FCSTD DOCUMENT  (FreeCAD 1.1R20251031 (Git shallow))
Label: generated_example_K93-10436_all7_withDockLinkFrame
License: All rights reserved
LicenseURL: https://en.wikipedia.org/wiki/All_rights_reserved
objects: App::FeaturePython×18, App::Link×15, App::Point×2, Assembly::AssemblyLink×1, Assembly::JointGroup×1, Assembly::AssemblyObject×1
EXTERNAL_REF file=K93-10436-H7-L120.FCStd obj=K93_120
EXTERNAL_REF file=Reference_all7.FCStd obj=Reference_all7_1
EXTERNAL_REF file=K93-10436-H7-L120_frontpanel_generated_example.FCStd obj=Body
EXTERNAL_REF file=K93-10436-H7-L120_Tarantinorino_right_withFeet.FCStd obj=Assembly
EXTERNAL_REF file=K93-10436-H7-L120_DockLink_Frame_example_mirrored.FCStd obj=Part__Mirroring
EXTERNAL_REF file=K93-10436-H7-L120_Bumperino.FCStd obj=Body
EXTERNAL_REF file=K93-10436-H7-L120_DockLink_Frame_example.FCStd obj=Body
EXTERNAL_REF file=3M_SJ5382.FCStd obj=Body

FEATURE [App::Link] K93_120  label="K93-120"
  LinkPlacement = pos=(0,126.938,111.562) rot=(1,0,0;1.5708rad)
  LinkedObject = -> <external K93-10436-H7-L120.FCStd>#K93_120
  Placement = pos=(0,126.938,111.562) rot=(1,0,0;1.5708rad)
FEATURE [App::FeaturePython] GroundedJoint  # Assembly grounded joint (typed FeaturePython)
  ObjectToGround = -> K93_120
  Placement = pos=(0,126.938,111.562) rot=(1,0,0;1.5708rad)
FEATURE [App::Link] Reference_all7_1  label="Reference_all7 1"
  LinkPlacement = pos=(2.87919,6.93809,110.59) rot=(0.99808,0,0;0rad)
  LinkedObject = -> <external Reference_all7.FCStd>#Reference_all7_1
  Placement = pos=(2.87919,6.93809,110.59) rot=(0.99808,0,0;0rad)
FEATURE [App::FeaturePython] Joint  label="Distance"  # Assembly joint (typed FeaturePython)
  Angle = 0
  AngleMax = 0
  AngleMin = 0
  Detach1 = false
  Detach2 = false
  Distance = -0.2
  Distance2 = 0
  EnableAngleMax = false
  EnableAngleMin = false
  EnableLengthMax = false
  EnableLengthMin = false
  JointType = 5 (Distance)
  LengthMax = 0
  LengthMin = 0
  Offset1 = pos=(0,0,0) rot=(0,0,1;3.14159rad)
  Placement1 = pos=(-50,10.1,0) rot=(-0.707107,0,0.707107;3.14159rad)
  Placement2 = pos=(-49.8,1.8e-15,0.755) rot=(-0.57735,-0.57735,0.57735;2.0944rad)
  Reference1 = -> Assembly [K93_120.Part__Feature.Face87,K93_120.Part__Feature.Vertex159]
  Reference2 = -> Assembly [Reference_all7_1.Part__Feature426.Face3,Reference_all7_1.Part__Feature426.Vertex3]
  Suppressed = false
FEATURE [App::FeaturePython] Joint001  label="Distance001"  # Assembly joint (typed FeaturePython)
  Angle = 0
  AngleMax = 0
  AngleMin = 0
  Detach1 = false
  Detach2 = false
  Distance = 0.2
  Distance2 = 0
  EnableAngleMax = false
  EnableAngleMin = false
  EnableLengthMax = false
  EnableLengthMin = false
  JointType = 5 (Distance)
  LengthMax = 0
  LengthMin = 0
  Placement1 = pos=(4e-16,-59.8,0.755) rot=(0,-0.707107,0.707107;3.14159rad)
  Placement2 = pos=(1.58751,4.42551,60) rot=(0,0,1;0rad)
  Reference1 = -> Assembly [Reference_all7_1.Part__Feature426.Face1,Reference_all7_1.Part__Feature426.Vertex4]
  Reference2 = -> Assembly [K93_120.Part__Feature.Face58,K93_120.Part__Feature.Vertex116]
  Suppressed = false
FEATURE [App::FeaturePython] Joint002  label="Distance002"  # Assembly joint (typed FeaturePython)
  Angle = 0
  AngleMax = 0
  AngleMin = 0
  Detach1 = false
  Detach2 = false
  Distance = 0.25
  Distance2 = 0
  EnableAngleMax = false
  EnableAngleMin = false
  EnableLengthMax = false
  EnableLengthMin = false
  JointType = 5 (Distance)
  LengthMax = 0
  LengthMin = 0
  Placement1 = pos=(-48.85,11.1,0) rot=(-0.57735,-0.57735,0.57735;4.18879rad)
  Placement2 = pos=(0.0111337,0.109635,1.51) rot=(0,0,1;0rad)
  Reference1 = -> Assembly [K93_120.Part__Feature.Face78,K93_120.Part__Feature.Vertex160]
  Reference2 = -> Assembly [Reference_all7_1.Part__Feature426.Face5,Reference_all7_1.Part__Feature426.Vertex3]
  Suppressed = false
FEATURE [App::Link] Body
  LinkPlacement = pos=(2.87919,-53.8119,119.256) rot=(1,0,0;1.5708rad)
  LinkedObject = -> <external K93-10436-H7-L120_frontpanel_generated_example.FCStd>#Body
  Placement = pos=(2.87919,-53.8119,119.256) rot=(1,0,0;1.5708rad)
FEATURE [App::FeaturePython] Joint003  label="Fixed"  # Assembly joint (typed FeaturePython)
  Angle = 0
  AngleMax = 0
  AngleMin = 0
  Detach1 = false
  Detach2 = false
  Distance = 0
  Distance2 = 0
  EnableAngleMax = false
  EnableAngleMin = false
  EnableLengthMax = false
  EnableLengthMin = false
  JointType = 0 (Fixed)
  LengthMax = 0
  LengthMin = 0
  Offset2 = pos=(0,0,0) rot=(0,0,1;3.14159rad)
  Placement1 = pos=(9.8e-15,0,60) rot=(0.707107,0,0.707107;3.14159rad)
  Placement2 = pos=(1.5046e-12,17.9943,-0.75) rot=(0,1,0;4.71239rad)
  Reference1 = -> Assembly [K93_120.Part__Feature001.Edge190,K93_120.Part__Feature001.Edge190]
  Reference2 = -> Assembly [Body.Edge39,Body.Edge39]
  Suppressed = false
FEATURE [App::Point] Origin001  label="Origin"
  Role = Origin
FEATURE [Assembly::AssemblyLink] Assembly004  label="Assembly"
  LinkedObject = -> <external K93-10436-H7-L120_Tarantinorino_right_withFeet.FCStd>#Assembly
  Origin = -> Origin008
  Placement = pos=(2.83915,-40.6619,129.251) rot=(0,0,1;0rad)
  Rigid = true
FEATURE [App::Point] Origin009  label="Origin011"
  Role = Origin
FEATURE [App::FeaturePython] Joint008  label="Fixed005"  # Assembly joint (typed FeaturePython)
  Angle = 0
  AngleMax = 0
  AngleMin = 0
  Detach1 = false
  Detach2 = false
  Distance = 0
  Distance2 = 0
  EnableAngleMax = false
  EnableAngleMin = false
  EnableLengthMax = false
  EnableLengthMin = false
  JointType = 0 (Fixed)
  LengthMax = 0
  LengthMin = 0
  Offset2 = pos=(0,0,0) rot=(0,0,1;3.14159rad)
  Placement2 = pos=(-47.3,-11.9443,0.75) rot=(0,1,0;3.14159rad)
  Reference1 = -> Assembly [Assembly004.Body__Mirror__1_001.Edge31,Assembly004.Body__Mirror__1_001.Edge31]
  Reference2 = -> Assembly [Body.Edge23,Body.Edge23]
  Suppressed = false
FEATURE [App::Link] Body__Mirror__1_  label="Body (Mirror #1)"
  LinkPlacement = pos=(2.85919,57.5381,130.16) rot=(0.998926,0,0;0rad)
  LinkedObject = -> <external K93-10436-H7-L120_DockLink_Frame_example_mirrored.FCStd>#Part__Mirroring
  Placement = pos=(2.85919,57.5381,130.16) rot=(0.998926,0,0;0rad)
FEATURE [App::FeaturePython] Joint009  label="Fixed010"  # Assembly joint (typed FeaturePython)
  Angle = 0
  AngleMax = 0
  AngleMin = 0
  Detach1 = false
  Detach2 = false
  Distance = 0
  Distance2 = 0
  EnableAngleMax = false
  EnableAngleMin = false
  EnableLengthMax = false
  EnableLengthMin = false
  JointType = 0 (Fixed)
  LengthMax = 0
  LengthMin = 0
  Offset2 = pos=(0,0,0) rot=(0,0,1;3.14159rad)
  Placement1 = pos=(-47.3,11.9443,0.75) rot=(-1,0,0;3.14159rad)
  Placement2 = pos=(47.32,10.9,1.04) rot=(0,-0.706347,0.706347;3.14159rad)
  Reference1 = -> Assembly [K93_120.Part__Feature003.Edge2,K93_120.Part__Feature003.Edge2]
  Reference2 = -> Assembly [Body__Mirror__1_.?Edge40,Body__Mirror__1_.?Edge40]
  Suppressed = false
FEATURE [App::Link] Body001
  LinkPlacement = pos=(2.87919,-56.1619,119.256) rot=(1,0,0;1.5708rad)
  LinkedObject = -> <external K93-10436-H7-L120_Bumperino.FCStd>#Body
  Placement = pos=(2.87919,-56.1619,119.256) rot=(1,0,0;1.5708rad)
FEATURE [App::Link] Body002
  LinkPlacement = pos=(2.87919,70.0381,119.256) rot=(0,0.707107,0.707107;3.14159rad)
  LinkedObject = -> <external K93-10436-H7-L120_Bumperino.FCStd>#Body
  Placement = pos=(2.87919,70.0381,119.256) rot=(0,0.707107,0.707107;3.14159rad)
FEATURE [App::Link] Body003
  LinkPlacement = pos=(2.83919,70.0381,119.256) rot=(-1,0,0;1.5708rad)
  LinkedObject = -> <external K93-10436-H7-L120_Bumperino.FCStd>#Body
  Placement = pos=(2.83919,70.0381,119.256) rot=(-1,0,0;1.5708rad)
FEATURE [App::Link] Body004
  LinkPlacement = pos=(2.91919,-56.1619,119.256) rot=(0,0.707107,-0.707107;3.14159rad)
  LinkedObject = -> <external K93-10436-H7-L120_Bumperino.FCStd>#Body
  Placement = pos=(2.91919,-56.1619,119.256) rot=(0,0.707107,-0.707107;3.14159rad)
FEATURE [App::FeaturePython] Joint012  label="Fixed013"  # Assembly joint (typed FeaturePython)
  Angle = 0
  AngleMax = 0
  AngleMin = 0
  Detach1 = false
  Detach2 = false
  Distance = 0
  Distance2 = 0
  EnableAngleMax = false
  EnableAngleMin = false
  EnableLengthMax = false
  EnableLengthMin = false
  JointType = 0 (Fixed)
  LengthMax = 0
  LengthMin = 0
  Placement1 = pos=(-47.32,12.5,1.04) rot=(0.998926,0,0;1.5708rad)
  Placement2 = pos=(-47.3,-11.9443,-1.42e-14) rot=(1,0,0;3.14159rad)
  Reference1 = -> Assembly [Body__Mirror__1_.?Edge65,Body__Mirror__1_.?Edge65]
  Reference2 = -> Assembly [Body003.Edge23,Body003.Edge23]
  Suppressed = false
FEATURE [App::FeaturePython] Joint013  label="Fixed014"  # Assembly joint (typed FeaturePython)
  Angle = 0
  AngleMax = 0
  AngleMin = 0
  Detach1 = false
  Detach2 = false
  Distance = 0
  Distance2 = 0
  EnableAngleMax = false
  EnableAngleMin = false
  EnableLengthMax = false
  EnableLengthMin = false
  JointType = 0 (Fixed)
  LengthMax = 0
  LengthMin = 0
  Offset2 = pos=(0,0,0) rot=(0,0,1;3.14159rad)
  Placement1 = pos=(47.32,12.5,1.04) rot=(0.998926,0,0;1.5708rad)
  Placement2 = pos=(-47.3,11.9443,-1.42e-14) rot=(0,0,1;3.14159rad)
  Reference1 = -> Assembly [Body__Mirror__1_.?Edge66,Body__Mirror__1_.?Edge66]
  Reference2 = -> Assembly [Body002.Edge22,Body002.Edge22]
  Suppressed = false
FEATURE [App::Link] Body005
  LinkPlacement = pos=(2.89919,-43.6619,130.16) rot=(0,0,1;0rad)
  LinkedObject = -> <external K93-10436-H7-L120_DockLink_Frame_example.FCStd>#Body
  Placement = pos=(2.89919,-43.6619,130.16) rot=(0,0,1;0rad)
FEATURE [App::FeaturePython] Joint014  label="Fixed016"  # Assembly joint (typed FeaturePython)
  Angle = 0
  AngleMax = 0
  AngleMin = 0
  Detach1 = false
  Detach2 = false
  Distance = 0
  Distance2 = 0
  EnableAngleMax = false
  EnableAngleMin = false
  EnableLengthMax = false
  EnableLengthMin = false
  JointType = 0 (Fixed)
  LengthMax = 0
  LengthMin = 0
  Placement1 = pos=(-47.3,11.9443,0.75) rot=(-1,0,0;3.14159rad)
  Placement2 = pos=(-47.32,-10.9,1.04) rot=(1,0,0;1.5708rad)
  Reference1 = -> Assembly [Body.Edge2,Body.Edge2]
  Reference2 = -> Assembly [Body005.?Edge39,Body005.?Edge39]
  Suppressed = false
FEATURE [App::FeaturePython] Joint015  label="Fixed017"  # Assembly joint (typed FeaturePython)
  Angle = 0
  AngleMax = 0
  AngleMin = 0
  Detach1 = false
  Detach2 = false
  Distance = 0
  Distance2 = 0
  EnableAngleMax = false
  EnableAngleMin = false
  EnableLengthMax = false
  EnableLengthMin = false
  JointType = 0 (Fixed)
  LengthMax = 0
  LengthMin = 0
  Placement1 = pos=(-47.32,-12.5,1.04) rot=(1,0,0;1.5708rad)
  Placement2 = pos=(-47.3,11.9443,7.1e-15) rot=(0,0,1;0rad)
  Reference1 = -> Assembly [Body005.?Edge65,Body005.?Edge65]
  Reference2 = -> Assembly [Body001.Edge22,Body001.Edge22]
  Suppressed = false
FEATURE [App::FeaturePython] Joint016  label="Fixed018"  # Assembly joint (typed FeaturePython)
  Angle = 0
  AngleMax = 0
  AngleMin = 0
  Detach1 = false
  Detach2 = false
  Distance = 0
  Distance2 = 0
  EnableAngleMax = false
  EnableAngleMin = false
  EnableLengthMax = false
  EnableLengthMin = false
  JointType = 0 (Fixed)
  LengthMax = 0
  LengthMin = 0
  Offset2 = pos=(0,0,0) rot=(0,0,1;3.14159rad)
  Placement1 = pos=(47.32,-12.5,1.04) rot=(1,0,0;1.5708rad)
  Placement2 = pos=(-47.3,-11.9443,0) rot=(0,1,0;3.14159rad)
  Reference1 = -> Assembly [Body005.?Edge66,Body005.?Edge66]
  Reference2 = -> Assembly [Body004.Face22,Body004.Edge1]
  Suppressed = false
FEATURE [App::Link] _3M_SJ5382  label="3M_SJ5382"
  LinkPlacement = pos=(37.4634,57.5381,91.16) rot=(1,0,0;3.14159rad)
  LinkedObject = -> <external 3M_SJ5382.FCStd>#Body
  Placement = pos=(37.4634,57.5381,91.16) rot=(1,0,0;3.14159rad)
FEATURE [App::Link] _3M_SJ5383  label="3M_SJ5383"
  LinkPlacement = pos=(-31.705,-43.6619,91.16) rot=(0,1,0;3.14159rad)
  LinkedObject = -> <external 3M_SJ5382.FCStd>#Body
  Placement = pos=(-31.705,-43.6619,91.16) rot=(0,1,0;3.14159rad)
FEATURE [App::Link] _3M_SJ5384  label="3M_SJ5384"
  LinkPlacement = pos=(-31.745,57.5381,91.16) rot=(1,0,0;3.14159rad)
  LinkedObject = -> <external 3M_SJ5382.FCStd>#Body
  Placement = pos=(-31.745,57.5381,91.16) rot=(1,0,0;3.14159rad)
FEATURE [App::Link] _3M_SJ5385  label="3M_SJ5385"
  LinkPlacement = pos=(37.5034,-43.6619,91.16) rot=(0,1,0;3.14159rad)
  LinkedObject = -> <external 3M_SJ5382.FCStd>#Body
  Placement = pos=(37.5034,-43.6619,91.16) rot=(0,1,0;3.14159rad)
FEATURE [App::Link] _3M_SJ5386  label="3M_SJ5386"
  LinkPlacement = pos=(-59.305,-43.6619,119.26) rot=(-0.707107,0,0.707107;3.14159rad)
  LinkedObject = -> <external 3M_SJ5382.FCStd>#Body
  Placement = pos=(-59.305,-43.6619,119.26) rot=(-0.707107,0,0.707107;3.14159rad)
FEATURE [App::Link] _3M_SJ5387  label="3M_SJ5387"
  LinkPlacement = pos=(-59.345,57.5381,119.26) rot=(-0.707107,0,0.707107;3.14159rad)
  LinkedObject = -> <external 3M_SJ5382.FCStd>#Body
  Placement = pos=(-59.345,57.5381,119.26) rot=(-0.707107,0,0.707107;3.14159rad)
FEATURE [App::FeaturePython] Joint017  label="Fixed019"  # Assembly joint (typed FeaturePython)
  Angle = 0
  AngleMax = 0
  AngleMin = 0
  Detach1 = false
  Detach2 = false
  Distance = 0
  Distance2 = 0
  EnableAngleMax = false
  EnableAngleMin = false
  EnableLengthMax = false
  EnableLengthMin = false
  JointType = 0 (Fixed)
  LengthMax = 0
  LengthMin = 0
  Placement1 = pos=(-34.6042,4.61512e-06,-39) rot=(0,1,0;3.14159rad)
  Placement2 = pos=(0,0,0) rot=(-1,0,0;3.14159rad)
  Reference1 = -> Assembly [Body005.?Face255,Body005.?Face255]
  Reference2 = -> Assembly [_3M_SJ5383.Edge4,_3M_SJ5383.Edge4]
  Suppressed = false
FEATURE [App::FeaturePython] Joint018  label="Fixed020"  # Assembly joint (typed FeaturePython)
  Angle = 0
  AngleMax = 0
  AngleMin = 0
  Detach1 = false
  Detach2 = false
  Distance = 0
  Distance2 = 0
  EnableAngleMax = false
  EnableAngleMin = false
  EnableLengthMax = false
  EnableLengthMin = false
  JointType = 0 (Fixed)
  LengthMax = 0
  LengthMin = 0
  Placement1 = pos=(34.6042,4.61512e-06,-39) rot=(1,0,0;3.14159rad)
  Placement2 = pos=(0,0,0) rot=(0,0,1;3.14159rad)
  Reference1 = -> Assembly [Body005.?Face256,Body005.?Face256]
  Reference2 = -> Assembly [_3M_SJ5385.Face3,_3M_SJ5385.Face3]
  Suppressed = false
FEATURE [App::FeaturePython] Joint019  label="Fixed021"  # Assembly joint (typed FeaturePython)
  Angle = 0
  AngleMax = 0
  AngleMin = 0
  Detach1 = false
  Detach2 = false
  Distance = 0
  Distance2 = 0
  EnableAngleMax = false
  EnableAngleMin = false
  EnableLengthMax = false
  EnableLengthMin = false
  JointType = 0 (Fixed)
  LengthMax = 0
  LengthMin = 0
  Placement1 = pos=(34.6042,-4.61512e-06,-39) rot=(-0.998926,0,0;0rad)
  Placement2 = pos=(0,0,0) rot=(-1,0,0;3.14159rad)
  Reference1 = -> Assembly [Body__Mirror__1_.?Face256,Body__Mirror__1_.?Face256]
  Reference2 = -> Assembly [_3M_SJ5382.Edge4,_3M_SJ5382.Edge4]
  Suppressed = false
FEATURE [App::FeaturePython] Joint020  label="Fixed022"  # Assembly joint (typed FeaturePython)
  Angle = 0
  AngleMax = 0
  AngleMin = 0
  Detach1 = false
  Detach2 = false
  Distance = 0
  Distance2 = 0
  EnableAngleMax = false
  EnableAngleMin = false
  EnableLengthMax = false
  EnableLengthMin = false
  JointType = 0 (Fixed)
  LengthMax = 0
  LengthMin = 0
  Placement1 = pos=(-34.6042,-4.61512e-06,-39) rot=(0,0,0.998926;3.14159rad)
  Placement2 = pos=(0,0,0) rot=(0,0,-1;3.14159rad)
  Reference1 = -> Assembly [Body__Mirror__1_.?Face255,Body__Mirror__1_.?Face255]
  Reference2 = -> Assembly [_3M_SJ5384.Face3,_3M_SJ5384.Face3]
  Suppressed = false
FEATURE [App::FeaturePython] Joint021  label="Fixed023"  # Assembly joint (typed FeaturePython)
  Angle = 0
  AngleMax = 0
  AngleMin = 0
  Detach1 = false
  Detach2 = false
  Distance = 0
  Distance2 = 0
  EnableAngleMax = false
  EnableAngleMin = false
  EnableLengthMax = false
  EnableLengthMin = false
  JointType = 0 (Fixed)
  LengthMax = 0
  LengthMin = 0
  Placement1 = pos=(0,0,0) rot=(0,0,-1;3.14159rad)
  Placement2 = pos=(-62.2042,-1.22189e-07,-10.9) rot=(0,-1,0;1.5708rad)
  Reference1 = -> Assembly [_3M_SJ5386.Face3,_3M_SJ5386.Face3]
  Reference2 = -> Assembly [Body005.?Face254,Body005.?Face254]
  Suppressed = false
FEATURE [App::FeaturePython] Joint022  label="Fixed024"  # Assembly joint (typed FeaturePython)
  Angle = 0
  AngleMax = 0
  AngleMin = 0
  Detach1 = false
  Detach2 = false
  Distance = 0
  Distance2 = 0
  EnableAngleMax = false
  EnableAngleMin = false
  EnableLengthMax = false
  EnableLengthMin = false
  JointType = 0 (Fixed)
  LengthMax = 0
  LengthMin = 0
  Placement1 = pos=(0,0,0) rot=(0,0,1;3.14159rad)
  Placement2 = pos=(-62.2042,0,-10.9) rot=(0.707107,0,0.707107;3.14159rad)
  Reference1 = -> Assembly [_3M_SJ5387.Face3,_3M_SJ5387.Face3]
  Reference2 = -> Assembly [Body__Mirror__1_.?Face254,Body__Mirror__1_.?Face254]
  Suppressed = false
FEATURE [Assembly::JointGroup] Joints
  Group = -> [GroundedJoint,Joint,Joint001,Joint002,Joint003,Joint008,Joint009,Joint012,Joint013,Joint014,Joint015,Joint016,Joint017,Joint018,Joint019,Joint020,Joint021,Joint022]
FEATURE [Assembly::AssemblyObject] Assembly
  Group = -> [Joints,K93_120,GroundedJoint,Reference_all7_1,Joint,Joint001,Joint002,Body,Joint003,Assembly004,Joint008,Body__Mirror__1_,Joint009,Body001,Body002,Body003,Body004,Joint012,Joint013,Body005,Joint014,Joint015,Joint016,_3M_SJ5382,_3M_SJ5383,_3M_SJ5384,_3M_SJ5385,_3M_SJ5386,_3M_SJ5387,Joint017,Joint018,Joint019,Joint020,Joint021,Joint022]
  Origin = -> Origin
  Type = Assembly

RESOLVED EXTERNAL PARTS (link-assembly join: the EXTERNAL_REF files above that resolve inside this repo's crawl, each included once):
---- part 3M_SJ5382.FCStd = doc fcstd_c030dc117f4a ----
FCSTD DOCUMENT  (FreeCAD 1.1R14555 (Git shallow))
Label: 3M_SJ5382
License: All rights reserved
LicenseURL: https://en.wikipedia.org/wiki/All_rights_reserved
objects: App::Point×1, Sketcher::SketchObject×1, PartDesign::Revolution×1, PartDesign::Body×1
note: 6 computed .brp shape members not serialized (recipe doc carries the construction recipe); baked Part::Feature solids carry a one-line shape summary decoded from their .brp

FEATURE [App::Point] Origin001
  Role = Origin
FEATURE [Sketcher::SketchObject] Sketch
  ArcFitTolerance = 1e-06
  AttachmentSupport = -> [Origin]
  ExternalTypes = [0]
  FullyConstrained = true
  MakeInternals = false
  MapMode = 5
  Placement = pos=(0,0,0) rot=(1,0,0;1.5708rad)
  sketch-geometry (5):
    g0: LineSegment StartX=0 StartY=0 StartZ=0 EndX=6.50065e-11 EndY=1.9 EndZ=0
    g1: LineSegment StartX=0 StartY=0 StartZ=0 EndX=3.17 EndY=0 EndZ=0
    g2: LineSegment StartX=3.17 StartY=0 StartZ=0 EndX=3.17 EndY=0.5 EndZ=0
    g3: ArcOfCircle CenterX=-1.10968e-05 CenterY=-2.38892 CenterZ=0 NormalX=0 NormalY=0 NormalZ=1 AngleXU=0 Radius=4.28892 StartAngle=0.739038 EndAngle=1.57079
    g4: LineSegment [constr] StartX=6.50065e-11 StartY=1.9 StartZ=0 EndX=2 EndY=1.9 EndZ=0
  constraints (15):
    c: Coincident(g0,g-1)
    c: PointOnObject(g0,g-2)
    c: Coincident(g1,g0)
    c: PointOnObject(g1,g-1)
    c: DistanceY(g0,g0) = 1.9
    c: Coincident(g2,g1)
    c: Vertical(g2)
    c: Coincident(g3,g0)
    c: Coincident(g3,g2)
    c: DistanceX(g1,g1) = 3.17
    c: DistanceY(g2,g2) = 0.5
    c: Coincident(g4,g0)
    c: Horizontal(g4)
    c: Tangent(g4,g3)
    c: DistanceX(g4,g4) = 2
FEATURE [PartDesign::Revolution] Revolution
  Angle = 360
  Angle2 = 0
  Axis = (0,2e-16,1)
  Base = (0,0,0)
  Profile = -> Sketch
  ReferenceAxis = -> Sketch [V_Axis]
  Refine = true
  Reversed = true
  Suppressed = false
  Type = 0
FEATURE [PartDesign::Body] Body  label="3M_SJ5382"
  AllowCompound = true
  Group = -> [Sketch,Revolution]
  Origin = -> Origin
  Tip = -> Revolution
---- part K93-10436-H7-L120_Bumperino.FCStd = doc fcstd_554f42e3a84f ----
FCSTD DOCUMENT  (FreeCAD 1.0R39319 (Git))
Label: K93-10436-H7-L120_Bumperino
License: All rights reserved
LicenseURL: https://en.wikipedia.org/wiki/All_rights_reserved
objects: Part::Feature×5, Sketcher::SketchObject×3, PartDesign::Pocket×2, App::DocumentObjectGroupPython×1, PartDesign::Pad×1, PartDesign::Mirrored×1, PartDesign::Body×1
note: 23 computed .brp shape members not serialized (recipe doc carries the construction recipe); baked Part::Feature solids carry a one-line shape summary decoded from their .brp

FEATURE [App::DocumentObjectGroupPython] LayerContainer  label="Layers"  # scripted group (container) (typed FeaturePython)
FEATURE [Part::Feature] Wire
  shape: bbox 3.2 x 3.2 x 2e-07 mm, 0 faces, 0 solids (baked)
FEATURE [Part::Feature] Wire001
  shape: bbox 3.2 x 3.2 x 2e-07 mm, 0 faces, 0 solids (baked)
FEATURE [Part::Feature] Wire002
  shape: bbox 3.2 x 3.2 x 2e-07 mm, 0 faces, 0 solids (baked)
FEATURE [Part::Feature] Wire003
  shape: bbox 3.2 x 3.2 x 2e-07 mm, 0 faces, 0 solids (baked)
FEATURE [Part::Feature] Wire004  label="PanelConture"
  shape: bbox 104 x 35.99 x 2e-07 mm, 0 faces, 0 solids (baked)
FEATURE [Sketcher::SketchObject] Sketch
  ArcFitTolerance = 1e-06
  FullyConstrained = true
  MakeInternals = false
  sketch-geometry (12):
    g0: ArcOfCircle CenterX=-46.1716 CenterY=15.9943 CenterZ=0 NormalX=0 NormalY=0 NormalZ=1 AngleXU=0 Radius=1.99973 StartAngle=1.5708 EndAngle=2.35633
    g1: LineSegment StartX=-47.5858 StartY=17.4081 StartZ=0 EndX=-51.4142 EndY=13.5801 EndZ=0
    g2: ArcOfCircle CenterX=-50 CenterY=12.1658 CenterZ=0 NormalX=0 NormalY=0 NormalZ=1 AngleXU=0 Radius=2 StartAngle=2.35619 EndAngle=3.14159
    g3: ArcOfCircle CenterX=-46.1716 CenterY=15.3778 CenterZ=0 NormalX=0 NormalY=0 NormalZ=1 AngleXU=0 Radius=2.6162 StartAngle=0.0358549 EndAngle=1.5708
    g4: LineSegment StartX=-43.5571 StartY=15.4716 StartZ=0 EndX=-43.3913 EndY=10.8516 EndZ=0
    g5: ArcOfCircle CenterX=-45.8905 CenterY=10.7619 CenterZ=0 NormalX=0 NormalY=0 NormalZ=1 AngleXU=0 Radius=2.50074 StartAngle=5.05273 EndAngle=6.31904
    g6: LineSegment StartX=-45.0557 StartY=8.40462 StartZ=0 EndX=-49.3762 EndY=6.87461 EndZ=0
    g7: ArcOfCircle CenterX=-48.9841 CenterY=5.76738 CenterZ=0 NormalX=0 NormalY=0 NormalZ=1 AngleXU=0 Radius=1.17461 StartAngle=1.91114 EndAngle=3.14159
    g8: LineSegment StartX=-50.1587 StartY=5.76738 StartZ=0 EndX=-50.1587 EndY=0 EndZ=0
    g9: LineSegment StartX=-50.1587 StartY=0 StartZ=0 EndX=-52 EndY=0 EndZ=0
    g10: LineSegment StartX=-52 StartY=12.1658 StartZ=0 EndX=-52 EndY=0 EndZ=0
    g11: Circle CenterX=-47.3 CenterY=11.9443 CenterZ=0 NormalX=0 NormalY=0 NormalZ=1 AngleXU=0 Radius=1.6
  constraints (22):
    c: Coincident(g0,g1)
    c: Coincident(g1,g2)
    c: Block(g0)
    c: Block(g1)
    c: Block(g2)
    c: PointOnObject(g8,g-1)
    c: Tangent(g7,g6) = -1.5708
    c: Tangent(g8,g7) = -1.5708
    c: Tangent(g6,g5) = 1.5708
    c: Tangent(g5,g4) = 1.5708
    c: Tangent(g4,g3) = 1.5708
    c: Coincident(g9,g8)
    c: Horizontal(g9)
    c: Tangent(g10,g2) = -1.5708
    c: Coincident(g10,g9)
    c: Vertical(g10)
    c: Block(g10)
    c: Block(g7)
    c: Block(g5)
    c: Tangent(g0,g3) = -1.5708
    c: Block(g3)
    c: Block(g11)
FEATURE [PartDesign::Pad] Pad  label="LengthBumper"
  Direction = (0,0,1)
  Length = 20
  Length2 = 10
  Profile = -> Sketch
  ReferenceAxis = -> Sketch [N_Axis]
  Refine = true
  Suppressed = false
  Type = 0
FEATURE [PartDesign::Mirrored] Mirrored
  BaseFeature = -> Pad
  MirrorPlane = -> Sketch [H_Axis]
  Originals = -> [Pad]
  Refine = true
  Suppressed = false
  TransformMode = 0
FEATURE [Sketcher::SketchObject] Sketch001
  ArcFitTolerance = 1e-06
  AttachmentSupport = -> [Mirrored]
  ExternalGeometry = -> [Mirrored]
  FullyConstrained = true
  MakeInternals = false
  MapMode = 5
  Placement = pos=(0,0,20) rot=(0,0,1;0rad)
  sketch-geometry (2):
    g0: Circle CenterX=-47.3 CenterY=11.9443 CenterZ=0 NormalX=0 NormalY=0 NormalZ=1 AngleXU=0 Radius=3
    g1: Circle CenterX=-47.3 CenterY=-11.9443 CenterZ=0 NormalX=0 NormalY=0 NormalZ=1 AngleXU=0 Radius=3
  constraints (4):
    c: Coincident(g0,g-3)
    c: Coincident(g1,g-4)
    c: Diameter(g1) = 6
    c: Equal(g0,g1)
FEATURE [PartDesign::Pocket] Pocket
  BaseFeature = -> Mirrored
  Direction = (0,0,-1)
  Length = 0
  Length2 = 5
  Offset = 5
  Profile = -> Sketch001
  ReferenceAxis = -> Sketch001 [N_Axis]
  Refine = true
  Suppressed = false
  Type = 3
  UpToFace = -> Mirrored [Face9]
FEATURE [Sketcher::SketchObject] Sketch002
  ArcFitTolerance = 1e-06
  AttachmentSupport = -> [XZ_Plane]
  ExternalGeometry = -> [Pocket]
  FullyConstrained = true
  MakeInternals = false
  MapMode = 5
  Placement = pos=(0,0,0) rot=(1,0,0;1.5708rad)
  sketch-geometry (3):
    g0: LineSegment StartX=-43.3913 StartY=20 StartZ=0 EndX=-52 EndY=20 EndZ=0
    g1: LineSegment StartX=-52 StartY=20 StartZ=0 EndX=-52 EndY=11.3914 EndZ=0
    g2: ArcOfCircle CenterX=-43.3913 CenterY=11.3913 CenterZ=0 NormalX=0 NormalY=0 NormalZ=1 AngleXU=0 Radius=8.60867 StartAngle=1.5708 EndAngle=3.14159
  constraints (8):
    c: Coincident(g0,g-3)
    c: Coincident(g0,g-5)
    c: Coincident(g1,g0)
    c: PointOnObject(g1,g-5)
    c: PointOnObject(g2,g-6)
    c: Coincident(g2,g1)
    c: Coincident(g2,g0)
    c: Tangent(g2,g-5)
FEATURE [PartDesign::Pocket] Pocket001
  BaseFeature = -> Pocket
  Direction = (0,1,-2e-16)
  Length = 5
  Length2 = 5
  Midplane = true
  Profile = -> Sketch002
  ReferenceAxis = -> Sketch002 [N_Axis]
  Refine = true
  Suppressed = false
  Type = 1
FEATURE [PartDesign::Body] Body
  AllowCompound = false
  Group = -> [Sketch,Pad,Mirrored,Sketch001,Pocket,Sketch002,Pocket001]
  Origin = -> Origin
  Placement = pos=(0,0,0) rot=(1,0,0;1.5708rad)
  Tip = -> Pocket001
---- part K93-10436-H7-L120_DockLink_Frame_example.FCStd = doc fcstd_989e58302a0f ----
FCSTD DOCUMENT  (FreeCAD 1.1R20251111 (Git shallow))
Label: K93-10436-H7-L120_DockLink_Frame_example
License: All rights reserved
LicenseURL: https://en.wikipedia.org/wiki/All_rights_reserved
objects: App::Link×7, PartDesign::Chamfer×2, Assembly::JointGroup×1, Part::MultiFuse×1, App::Point×1, PartDesign::FeatureBase×1, PartDesign::Body×1
note: 10 computed .brp shape members not serialized (recipe doc carries the construction recipe); baked Part::Feature solids carry a one-line shape summary decoded from their .brp
EXTERNAL_REF file=K93-10436-H7-L120_DockLink_Frame.FCStd obj=Body
EXTERNAL_REF file=../../FreeCAD_DElements/DockLink/DockLink_male.FCStd obj=Body
EXTERNAL_REF file=../../FreeCAD_DElements/DockLink/DockLink_female.FCStd obj=Body

FEATURE [Assembly::JointGroup] Joints
FEATURE [App::Link] K93_10436_H7_L120_DockLink_Frame  label="K93-10436-H7-L120_DockLink_Frame"
  LinkPlacement = pos=(0,-10.9,-10.9) rot=(1,0,0;1.5708rad)
  LinkedObject = -> <external K93-10436-H7-L120_DockLink_Frame.FCStd>#Body
  Placement = pos=(0,-10.9,-10.9) rot=(1,0,0;1.5708rad)
FEATURE [App::Link] Body_DockLink_male
  LinkPlacement = pos=(34.6042,3.94077e-06,-35) rot=(1,0,0;3.14159rad)
  LinkedObject = -> <external ../../FreeCAD_DElements/DockLink/DockLink_male.FCStd>#Body
  Placement = pos=(34.6042,3.94077e-06,-35) rot=(1,0,0;3.14159rad)
FEATURE [App::Link] Body_DockLink_male001
  LinkPlacement = pos=(-34.6042,3.94077e-06,-35) rot=(0,1,0;3.14159rad)
  LinkedObject = -> <external ../../FreeCAD_DElements/DockLink/DockLink_male.FCStd>#Body
  Placement = pos=(-34.6042,3.94077e-06,-35) rot=(0,1,0;3.14159rad)
FEATURE [App::Link] Body_DockLink_male002
  LinkPlacement = pos=(-58.2042,-1.22189e-07,-10.9) rot=(0,1,0;4.71239rad)
  LinkedObject = -> <external ../../FreeCAD_DElements/DockLink/DockLink_male.FCStd>#Body
  Placement = pos=(-58.2042,-1.22189e-07,-10.9) rot=(0,1,0;4.71239rad)
FEATURE [App::Link] Body_DockLink_female
  LinkPlacement = pos=(34.6042,-3.17362e-06,7.2) rot=(1,0,0;0rad)
  LinkedObject = -> <external ../../FreeCAD_DElements/DockLink/DockLink_female.FCStd>#Body
  Placement = pos=(34.6042,-3.17362e-06,7.2) rot=(1,0,0;0rad)
FEATURE [App::Link] Body_DockLink_female002
  LinkPlacement = pos=(-34.6042,-3.17362e-06,7.2) rot=(1,0,0;0rad)
  LinkedObject = -> <external ../../FreeCAD_DElements/DockLink/DockLink_female.FCStd>#Body
  Placement = pos=(-34.6042,-3.17362e-06,7.2) rot=(1,0,0;0rad)
FEATURE [App::Link] Body_DockLink_female003
  LinkPlacement = pos=(52.2042,-1.22189e-07,-10.9) rot=(0,1,0;1.5708rad)
  LinkedObject = -> <external ../../FreeCAD_DElements/DockLink/DockLink_female.FCStd>#Body
  Placement = pos=(52.2042,-1.22189e-07,-10.9) rot=(0,1,0;1.5708rad)
FEATURE [Part::MultiFuse] Fusion
  Refine = true
  Shapes = -> [K93_10436_H7_L120_DockLink_Frame,Body_DockLink_male,Body_DockLink_male001,Body_DockLink_male002,Body_DockLink_female,Body_DockLink_female002,Body_DockLink_female003]
FEATURE [App::Point] Origin005  label="Origin006"
  Role = Origin
FEATURE [PartDesign::FeatureBase] BaseFeature
  BaseFeature = -> Fusion
  Suppressed = false
FEATURE [PartDesign::Chamfer] Chamfer
  Angle = 45
  Base = -> BaseFeature [Edge186,Edge341,Edge191,Edge207,Edge211,Edge212,Edge219,Edge234,Edge349,Edge348,Edge347,Edge346,Edge345,Edge344,Edge343,Edge342,Edge236,Edge221,Edge214,Edge210,Edge206,Edge193,Edge184,Edge494,Edge376,Edge367,Edge356,Edge354,Edge350,Edge357,Edge365,Edge493,Edge49]
  BaseFeature = -> BaseFeature
  ChamferType = 0
  FlipDirection = false
  Refine = true
  Size = 1
  Size2 = 1
  SupportTransform = false
  Suppressed = false
  UseAllEdges = false
FEATURE [PartDesign::Chamfer] Chamfer001
  Angle = 45
  Base = -> Chamfer [Edge285,Edge289,Edge321,Edge325,Edge287,Edge337,Edge341,Edge351,Edge338,Edge312,Edge308,Edge299]
  BaseFeature = -> Chamfer
  ChamferType = 0
  FlipDirection = false
  Refine = true
  Size = 1
  Size2 = 1
  SupportTransform = false
  Suppressed = false
  UseAllEdges = false
FEATURE [PartDesign::Body] Body
  AllowCompound = true
  BaseFeature = -> Fusion
  Group = -> [BaseFeature,Chamfer,Chamfer001]
  Origin = -> Origin004
  Tip = -> Chamfer001
---- part K93-10436-H7-L120_DockLink_Frame_example_mirrored.FCStd = doc fcstd_caa51bdad4e9 ----
FCSTD DOCUMENT  (FreeCAD 1.1R20251031 (Git shallow))
Label: K93-10436-H7-L120_DockLink_Frame_example_mirrored
License: All rights reserved
LicenseURL: https://en.wikipedia.org/wiki/All_rights_reserved
objects: App::Link×7, PartDesign::Chamfer×2, Assembly::JointGroup×1, Part::MultiFuse×1, App::Point×1, PartDesign::FeatureBase×1, PartDesign::Body×1, Part::Mirroring×1
note: 11 computed .brp shape members not serialized (recipe doc carries the construction recipe); baked Part::Feature solids carry a one-line shape summary decoded from their .brp
EXTERNAL_REF file=K93-10436-H7-L120_DockLink_Frame.FCStd obj=Body
EXTERNAL_REF file=../../FreeCAD_DElements/DockLink/DockLink_male.FCStd obj=Body
EXTERNAL_REF file=../../FreeCAD_DElements/DockLink/DockLink_female.FCStd obj=Body

FEATURE [Assembly::JointGroup] Joints
FEATURE [App::Link] K93_10436_H7_L120_DockLink_Frame  label="K93-10436-H7-L120_DockLink_Frame"
  LinkPlacement = pos=(0,-10.9,-10.9) rot=(1,0,0;1.5708rad)
  LinkedObject = -> <external K93-10436-H7-L120_DockLink_Frame.FCStd>#Body
  Placement = pos=(0,-10.9,-10.9) rot=(1,0,0;1.5708rad)
FEATURE [App::Link] Body_DockLink_male
  LinkPlacement = pos=(34.6042,3.94077e-06,-35) rot=(1,0,0;3.14159rad)
  LinkedObject = -> <external ../../FreeCAD_DElements/DockLink/DockLink_male.FCStd>#Body
  Placement = pos=(34.6042,3.94077e-06,-35) rot=(1,0,0;3.14159rad)
FEATURE [App::Link] Body_DockLink_male001
  LinkPlacement = pos=(-34.6042,3.94077e-06,-35) rot=(0,1,0;3.14159rad)
  LinkedObject = -> <external ../../FreeCAD_DElements/DockLink/DockLink_male.FCStd>#Body
  Placement = pos=(-34.6042,3.94077e-06,-35) rot=(0,1,0;3.14159rad)
FEATURE [App::Link] Body_DockLink_male002
  LinkPlacement = pos=(-58.2042,-1.22189e-07,-10.9) rot=(0,1,0;4.71239rad)
  LinkedObject = -> <external ../../FreeCAD_DElements/DockLink/DockLink_male.FCStd>#Body
  Placement = pos=(-58.2042,-1.22189e-07,-10.9) rot=(0,1,0;4.71239rad)
FEATURE [App::Link] Body_DockLink_female
  LinkPlacement = pos=(34.6042,-3.17362e-06,7.2) rot=(1,0,0;0rad)
  LinkedObject = -> <external ../../FreeCAD_DElements/DockLink/DockLink_female.FCStd>#Body
  Placement = pos=(34.6042,-3.17362e-06,7.2) rot=(1,0,0;0rad)
FEATURE [App::Link] Body_DockLink_female002
  LinkPlacement = pos=(-34.6042,-3.17362e-06,7.2) rot=(1,0,0;0rad)
  LinkedObject = -> <external ../../FreeCAD_DElements/DockLink/DockLink_female.FCStd>#Body
  Placement = pos=(-34.6042,-3.17362e-06,7.2) rot=(1,0,0;0rad)
FEATURE [App::Link] Body_DockLink_female003
  LinkPlacement = pos=(52.2042,-1.22189e-07,-10.9) rot=(0,1,0;1.5708rad)
  LinkedObject = -> <external ../../FreeCAD_DElements/DockLink/DockLink_female.FCStd>#Body
  Placement = pos=(52.2042,-1.22189e-07,-10.9) rot=(0,1,0;1.5708rad)
FEATURE [Part::MultiFuse] Fusion
  Refine = true
  Shapes = -> [K93_10436_H7_L120_DockLink_Frame,Body_DockLink_male,Body_DockLink_male001,Body_DockLink_male002,Body_DockLink_female,Body_DockLink_female002,Body_DockLink_female003]
FEATURE [App::Point] Origin005  label="Origin006"
  Role = Origin
FEATURE [PartDesign::FeatureBase] BaseFeature
  BaseFeature = -> Fusion
  Suppressed = false
FEATURE [PartDesign::Chamfer] Chamfer
  Angle = 45
  Base = -> BaseFeature [Edge186,Edge341,Edge191,Edge207,Edge211,Edge212,Edge219,Edge234,Edge349,Edge348,Edge347,Edge346,Edge345,Edge344,Edge343,Edge342,Edge236,Edge221,Edge214,Edge210,Edge206,Edge193,Edge184,Edge494,Edge376,Edge367,Edge356,Edge354,Edge350,Edge357,Edge365,Edge493,Edge49]
  BaseFeature = -> BaseFeature
  ChamferType = 0
  FlipDirection = false
  Refine = true
  Size = 1
  Size2 = 1
  SupportTransform = false
  Suppressed = false
  UseAllEdges = false
FEATURE [PartDesign::Chamfer] Chamfer001
  Angle = 45
  Base = -> Chamfer [Edge351,Edge341,Edge338,Edge312,Edge308,Edge299,Edge287,Edge285,Edge289,Edge321,Edge325,Edge337]
  BaseFeature = -> Chamfer
  ChamferType = 0
  FlipDirection = false
  Refine = true
  Size = 1
  Size2 = 1
  SupportTransform = false
  Suppressed = false
  UseAllEdges = false
FEATURE [PartDesign::Body] Body
  AllowCompound = true
  BaseFeature = -> Fusion
  Group = -> [BaseFeature,Chamfer,Chamfer001]
  Origin = -> Origin004
  Tip = -> Chamfer001
FEATURE [Part::Mirroring] Part__Mirroring  label="Body (Mirror #1)"
  Base = (0,0,0)
  Normal = (0,1,0)
  Source = -> Body
---- part K93-10436-H7-L120_Tarantinorino_right_withFeet.FCStd = doc fcstd_a3d1782a5d18 ----
FCSTD DOCUMENT  (FreeCAD 1.1R20251031 (Git shallow))
Label: K93-10436-H7-L120_Tarantinorino_right_withFeet
License: All rights reserved
LicenseURL: https://en.wikipedia.org/wiki/All_rights_reserved
objects: App::Link×3, App::FeaturePython×3, App::Point×1, Assembly::JointGroup×1, Assembly::AssemblyObject×1
EXTERNAL_REF file=K93-10436-H7-L120_Tarantinorino_right.FCStd obj=Part__Mirroring
EXTERNAL_REF file=3M_SJ5382.FCStd obj=Body

FEATURE [App::Point] Origin001
  Role = Origin
FEATURE [App::Link] Body__Mirror__1_  label="Body (Mirror #1)"
  LinkPlacement = pos=(1.43051e-06,-13.9,-10.1) rot=(1,0,0;1.5708rad)
  LinkedObject = -> <external K93-10436-H7-L120_Tarantinorino_right.FCStd>#Part__Mirroring
  Placement = pos=(1.43051e-06,-13.9,-10.1) rot=(1,0,0;1.5708rad)
FEATURE [App::FeaturePython] GroundedJoint  # Assembly grounded joint (typed FeaturePython)
  ObjectToGround = -> Body__Mirror__1_
FEATURE [App::Link] _3M_SJ5382  label="3M_SJ5382"
  LinkPlacement = pos=(-31.32,-1.89999,-37) rot=(0.707107,0.707107,0;3.14159rad)
  LinkedObject = -> <external 3M_SJ5382.FCStd>#Body
  Placement = pos=(-31.32,-1.89999,-37) rot=(0.707107,0.707107,0;3.14159rad)
FEATURE [App::FeaturePython] Joint  label="Fixed"  # Assembly joint (typed FeaturePython)
  Angle = 0
  AngleMax = 0
  AngleMin = 0
  Detach1 = false
  Detach2 = false
  Distance = 0
  Distance2 = 0
  EnableAngleMax = false
  EnableAngleMin = false
  EnableLengthMax = false
  EnableLengthMin = false
  JointType = 0 (Fixed)
  LengthMax = 0
  LengthMin = 0
  Placement1 = pos=(-31.32,-26.9,-12) rot=(-0.57735,0.57735,-0.57735;4.18879rad)
  Placement2 = pos=(0,0,0) rot=(0,0,-1;3.14159rad)
  Reference1 = -> Assembly [Body__Mirror__1_.Face111,Body__Mirror__1_.Face111]
  Reference2 = -> Assembly [_3M_SJ5382.?Face3,_3M_SJ5382.?Edge1]
  Suppressed = false
FEATURE [App::Link] _3M_SJ5383  label="3M_SJ5383"
  LinkPlacement = pos=(-52.7042,-1.9,-10.1) rot=(-0.57735,-0.57735,0.57735;2.0944rad)
  LinkedObject = -> <external 3M_SJ5382.FCStd>#Body
  Placement = pos=(-52.7042,-1.9,-10.1) rot=(-0.57735,-0.57735,0.57735;2.0944rad)
FEATURE [App::FeaturePython] Joint001  label="Fixed001"  # Assembly joint (typed FeaturePython)
  Angle = 0
  AngleMax = 0
  AngleMin = 0
  Detach1 = false
  Detach2 = false
  Distance = 0
  Distance2 = 0
  EnableAngleMax = false
  EnableAngleMin = false
  EnableLengthMax = false
  EnableLengthMin = false
  JointType = 0 (Fixed)
  LengthMax = 0
  LengthMin = 0
  Placement1 = pos=(-52.7042,0,-12) rot=(-0.707107,0,-0.707107;3.14159rad)
  Placement2 = pos=(0,0,0) rot=(0,0,1;3.14159rad)
  Reference1 = -> Assembly [Body__Mirror__1_.Face106,Body__Mirror__1_.Face106]
  Reference2 = -> Assembly [_3M_SJ5383.?Face3,_3M_SJ5383.?Face3]
  Suppressed = false
FEATURE [Assembly::JointGroup] Joints
  Group = -> [GroundedJoint,Joint,Joint001]
FEATURE [Assembly::AssemblyObject] Assembly
  Group = -> [Joints,Body__Mirror__1_,GroundedJoint,_3M_SJ5382,Joint,_3M_SJ5383,Joint001]
  Origin = -> Origin
  Type = Assembly
---- part K93-10436-H7-L120_frontpanel_generated_example.FCStd = doc fcstd_f3005fab9b42 ----
FCSTD DOCUMENT  (FreeCAD 1.1R14555 (Git shallow))
Label: K93-10436-H7-L120_frontpanel_generated_example
License: All rights reserved
LicenseURL: https://en.wikipedia.org/wiki/All_rights_reserved
objects: Part::Feature×1, PartDesign::FeatureBase×1, Sketcher::SketchObject×1, PartDesign::Pocket×1, PartDesign::Body×1, App::Point×1
note: 9 computed .brp shape members not serialized (recipe doc carries the construction recipe); baked Part::Feature solids carry a one-line shape summary decoded from their .brp

FEATURE [Part::Feature] Part__Feature  label="K93-B"
  shape: bbox 104 x 35.99 x 1.5 mm, 34 faces (baked)
FEATURE [PartDesign::FeatureBase] BaseFeature
  BaseFeature = -> Part__Feature
  Suppressed = false
FEATURE [Sketcher::SketchObject] Sketch
  ArcFitTolerance = 1e-06
  AttachmentSupport = -> [BaseFeature]
  ExternalTypes = [0]
  FullyConstrained = false
  MakeInternals = false
  MapMode = 5
  Placement = pos=(0,0,0.75) rot=(0,0,1;0rad)
  sketch-geometry (7):
    g0: Circle CenterX=-40.64 CenterY=2.6 CenterZ=0 NormalX=0 NormalY=0 NormalZ=1 AngleXU=0 Radius=3.15
    g1: Circle CenterX=-26.66 CenterY=2.72 CenterZ=0 NormalX=0 NormalY=0 NormalZ=1 AngleXU=0 Radius=6.5
    g2: Circle CenterX=-11.43 CenterY=1.92 CenterZ=0 NormalX=0 NormalY=0 NormalZ=1 AngleXU=0 Radius=5.75
    g3: Circle CenterX=1.29 CenterY=-0.88 CenterZ=0 NormalX=0 NormalY=0 NormalZ=1 AngleXU=0 Radius=1.8
    g4: Circle CenterX=13.97 CenterY=0.62 CenterZ=0 NormalX=0 NormalY=0 NormalZ=1 AngleXU=0 Radius=3.5
    g5: Circle CenterX=26.67 CenterY=2.6 CenterZ=0 NormalX=0 NormalY=0 NormalZ=1 AngleXU=0 Radius=3.15
    g6: Circle CenterX=35.56 CenterY=-1.85 CenterZ=0 NormalX=0 NormalY=0 NormalZ=1 AngleXU=0 Radius=2.6
FEATURE [PartDesign::Pocket] Pocket
  BaseFeature = -> BaseFeature
  Direction = (0,0,-1)
  Length = 5
  Length2 = 5
  Profile = -> Sketch
  ReferenceAxis = -> Sketch [N_Axis]
  Refine = true
  SideType = 0
  Suppressed = false
  Type = 1
  Type2 = 0
FEATURE [PartDesign::Body] Body
  AllowCompound = false
  BaseFeature = -> Part__Feature
  Group = -> [BaseFeature,Sketch,Pocket]
  Origin = -> Origin
  Tip = -> Pocket
FEATURE [App::Point] Origin001  label="Origin"
  Role = Origin
